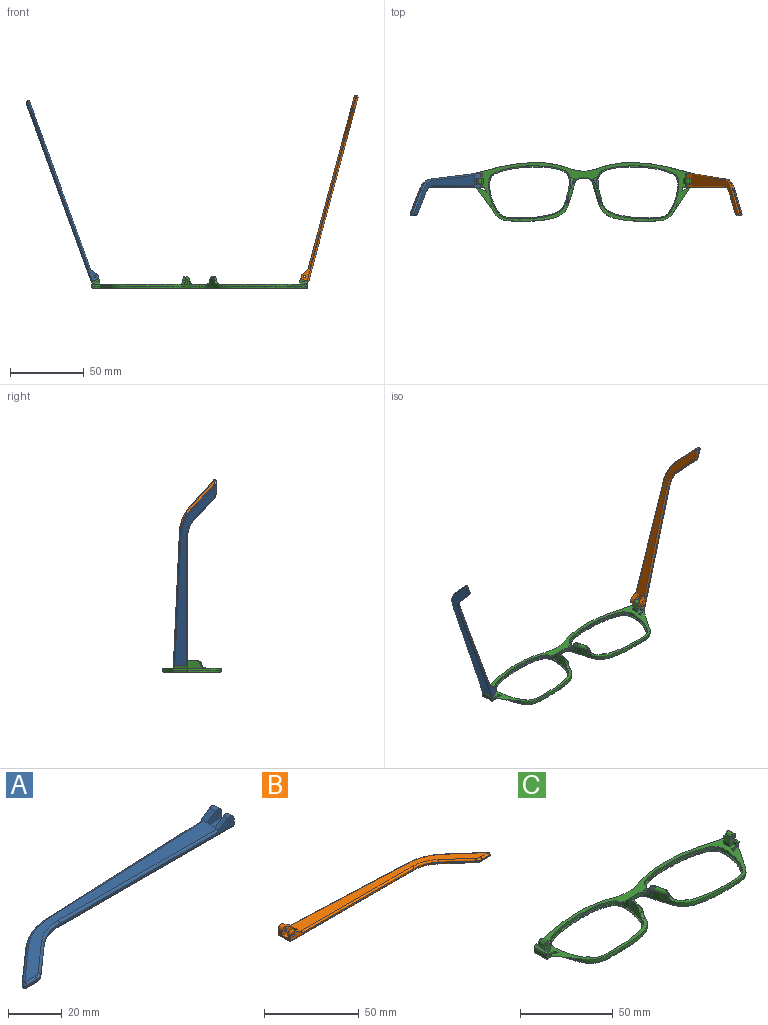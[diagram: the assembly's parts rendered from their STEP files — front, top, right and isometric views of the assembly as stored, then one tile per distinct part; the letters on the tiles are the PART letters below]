
ASSEMBLY  parts=3 mates=2
PART A: 43 faces, bbox 130.2x29.5x5.9 mm
  f0: plane 9.62x3.72mm, normal (1,0,0), area 24.7mm2, adj f1,f3,f4,f5,f10,f16,f18,f28
  f1: cylinder r=2.2mm len=3.45mm, axis (0,-1,0), area 11mm2, adj f0,f2,f4,f37
  f2: plane 6.01x3.91mm, normal (-0.55,0,0.84), area 12.7mm2, adj f1,f4,f9,f19,f37
  f3: plane 2.26x0.1mm, normal (0,0,1), area 0.1mm2, adj f0,f5,f18
  f4: plane 92.1x4.9mm, normal (0,-1,0), area 79.9mm2, adj f0,f1,f2,f14,f19,f36,f42
  f5: plane 93.42x4.13mm, normal (-0.04,1,0), area 64.8mm2, adj f0,f3,f11,f15,f17,f27,f28
  f6: plane 17.82x15.72mm, normal (-0.66,0.75,0), area 14.3mm2, adj f11,f12,f25,f30
  f7: plane 5.46x0.6mm, normal (0,-1,0), area 3.3mm2, adj f12,f13,f23,f32
  f8: plane 14.99x13.23mm, normal (0.66,-0.75,0), area 12mm2, adj f13,f14,f21,f34
  f9: plane 121.18x26.73mm, normal (0,0,1), area 627.7mm2, adj f2,f17,f19,f20,f21,f22,f23,f25
  f10: plane 129.1x27.08mm, normal (0,0,-1), area 686.5mm2, adj f0,f28,f29,f30,f32,f33,f34,f35
  f11: cylinder r=30mm len=18.52mm, axis (0,0,-1), area 12.2mm2, adj f5,f6,f26,f29
  f12: cylinder r=1mm len=1.75mm, axis (0,0,-1), area 1.5mm2, adj f6,f7,f24,f31
  f13: cylinder r=5mm len=3.31mm, axis (0,0,-1), area 2.2mm2, adj f7,f8,f22,f33
  f14: cylinder r=20mm len=13.23mm, axis (0,0,1), area 8.7mm2, adj f4,f8,f20,f35
  f15: plane 5.66x0.25mm, normal (0,0,-1), area 0.7mm2, adj f5,f17,f18
  f16: cylinder r=2.2mm len=3.45mm, axis (0,-1,0), area 14.8mm2, adj f0,f17,f18,f38
  f17: plane 6.01x3.91mm, normal (-0.55,0,0.84), area 16.9mm2, adj f5,f9,f15,f16,f18,f27,f38
  f18: plane 7.92x3.3mm, normal (0,1,0), area 15.9mm2, adj f0,f3,f15,f16,f17,f41
  f19: cylinder r=1mm len=84.18mm, axis (-1,0,0), area 131.4mm2, adj f2,f4,f9,f20
  f20: torus R=21mm, axis (0,0,1), area 23.1mm2, adj f9,f14,f19,f21
  f21: cylinder r=1mm len=15.65mm, axis (-0.75,-0.66,0), area 31.4mm2, adj f8,f9,f20,f22
  f22: torus R=4mm, axis (0,0,1), area 5.3mm2, adj f9,f13,f21,f23
  f23: cylinder r=1mm len=5.46mm, axis (-1,0,0), area 8.6mm2, adj f7,f9,f22,f24
  f24: sphere r=1mm, area 2.4mm2, adj f12,f23,f25
  f25: cylinder r=1mm len=18.48mm, axis (0.75,0.66,0), area 37.3mm2, adj f6,f9,f24,f26
  f26: torus R=29mm, axis (0,0,1), area 31.6mm2, adj f9,f11,f25,f27
  f27: cylinder r=1mm len=85.5mm, axis (1,0.04,0), area 133.5mm2, adj f5,f9,f17,f26
  f28: cylinder r=1mm len=93.46mm, axis (-1,-0.04,0), area 146.9mm2, adj f0,f5,f10,f29
  f29: torus R=29mm, axis (0,0,1), area 31.6mm2, adj f10,f11,f28,f30
  f30: cylinder r=1mm len=18.48mm, axis (-0.75,-0.66,0), area 37.3mm2, adj f6,f10,f29,f31
  f31: sphere r=1mm, area 2.4mm2, adj f12,f30,f32
  f32: cylinder r=1mm len=5.46mm, axis (1,0,0), area 8.6mm2, adj f7,f10,f31,f33
  f33: torus R=4mm, axis (0,0,1), area 5.3mm2, adj f10,f13,f32,f34
  f34: cylinder r=1mm len=15.65mm, axis (0.75,0.66,0), area 31.4mm2, adj f8,f10,f33,f35
  f35: torus R=21mm, axis (0,0,1), area 23.1mm2, adj f10,f14,f34,f36
  f36: cylinder r=1mm len=92.1mm, axis (1,0,0), area 144.7mm2, adj f0,f4,f10,f35
  f37: plane 7.92x4.7mm, normal (0,1,0), area 27mm2, adj f0,f1,f2,f39,f40,f42
  f38: plane 7.92x4.7mm, normal (0,-1,0), area 27mm2, adj f0,f16,f17,f39,f40,f41
  f39: plane 7.92x4.1mm, normal (0,0,1), area 32.5mm2, adj f0,f37,f38,f40
  f40: plane 4.1x1.4mm, normal (1,0,0), area 5.7mm2, adj f9,f37,f38,f39
  f41: cylinder r=0.5mm len=3.1mm, axis (0,-1,0), area 9.7mm2, adj f18,f38
  f42: cylinder r=0.5mm len=2.3mm, axis (0,-1,0), area 7.2mm2, adj f4,f37
PART B: 43 faces, bbox 130.2x29.5x5.9 mm
  f0: plane 9.62x3.72mm, normal (-1,0,0), area 24.7mm2, adj f1,f3,f4,f5,f10,f16,f18,f28
  f1: cylinder r=2.2mm len=3.45mm, axis (0,-1,0), area 11mm2, adj f0,f2,f4,f37
  f2: plane 6.01x3.91mm, normal (0.55,0,0.84), area 12.7mm2, adj f1,f4,f9,f19,f37
  f3: plane 2.26x0.1mm, normal (0,0,1), area 0.1mm2, adj f0,f5,f18
  f4: plane 92.1x4.9mm, normal (0,-1,0), area 78.2mm2, adj f0,f1,f2,f14,f19,f36,f42
  f5: plane 93.42x4.13mm, normal (0.04,1,0), area 64.8mm2, adj f0,f3,f11,f15,f17,f27,f28
  f6: plane 17.82x15.72mm, normal (0.66,0.75,0), area 14.3mm2, adj f11,f12,f25,f30
  f7: plane 5.46x0.6mm, normal (0,-1,0), area 3.3mm2, adj f12,f13,f23,f32
  f8: plane 14.99x13.23mm, normal (-0.66,-0.75,0), area 12mm2, adj f13,f14,f21,f34
  f9: plane 121.18x26.73mm, normal (0,0,1), area 627.7mm2, adj f2,f17,f19,f20,f21,f22,f23,f25
  f10: plane 129.1x27.08mm, normal (0,0,-1), area 686.5mm2, adj f0,f28,f29,f30,f32,f33,f34,f35
  f11: cylinder r=30mm len=18.52mm, axis (0,0,-1), area 12.2mm2, adj f5,f6,f26,f29
  f12: cylinder r=1mm len=1.75mm, axis (0,0,-1), area 1.5mm2, adj f6,f7,f24,f31
  f13: cylinder r=5mm len=3.31mm, axis (0,0,-1), area 2.2mm2, adj f7,f8,f22,f33
  f14: cylinder r=20mm len=13.23mm, axis (0,0,1), area 8.7mm2, adj f4,f8,f20,f35
  f15: plane 5.66x0.25mm, normal (0,0,-1), area 0.7mm2, adj f5,f17,f18
  f16: cylinder r=2.2mm len=3.45mm, axis (0,-1,0), area 14.8mm2, adj f0,f17,f18,f38
  f17: plane 6.01x3.91mm, normal (0.55,0,0.84), area 16.9mm2, adj f5,f9,f15,f16,f18,f27,f38
  f18: plane 7.92x3.3mm, normal (0,1,0), area 14.3mm2, adj f0,f3,f15,f16,f17,f41
  f19: cylinder r=1mm len=84.18mm, axis (1,0,0), area 131.4mm2, adj f2,f4,f9,f20
  f20: torus R=21mm, axis (0,0,1), area 23.1mm2, adj f9,f14,f19,f21
  f21: cylinder r=1mm len=15.65mm, axis (0.75,-0.66,0), area 31.4mm2, adj f8,f9,f20,f22
  f22: torus R=4mm, axis (0,0,1), area 5.3mm2, adj f9,f13,f21,f23
  f23: cylinder r=1mm len=5.46mm, axis (1,0,0), area 8.6mm2, adj f7,f9,f22,f24
  f24: sphere r=1mm, area 2.4mm2, adj f12,f23,f25
  f25: cylinder r=1mm len=18.48mm, axis (-0.75,0.66,0), area 37.3mm2, adj f6,f9,f24,f26
  f26: torus R=29mm, axis (0,0,1), area 31.6mm2, adj f9,f11,f25,f27
  f27: cylinder r=1mm len=85.5mm, axis (-1,0.04,0), area 133.5mm2, adj f5,f9,f17,f26
  f28: cylinder r=1mm len=93.46mm, axis (1,-0.04,0), area 146.9mm2, adj f0,f5,f10,f29
  f29: torus R=29mm, axis (0,0,1), area 31.6mm2, adj f10,f11,f28,f30
  f30: cylinder r=1mm len=18.48mm, axis (0.75,-0.66,0), area 37.3mm2, adj f6,f10,f29,f31
  f31: sphere r=1mm, area 2.4mm2, adj f12,f30,f32
  f32: cylinder r=1mm len=5.46mm, axis (-1,0,0), area 8.6mm2, adj f7,f10,f31,f33
  f33: torus R=4mm, axis (0,0,1), area 5.3mm2, adj f10,f13,f32,f34
  f34: cylinder r=1mm len=15.65mm, axis (-0.75,0.66,0), area 31.4mm2, adj f8,f10,f33,f35
  f35: torus R=21mm, axis (0,0,1), area 23.1mm2, adj f10,f14,f34,f36
  f36: cylinder r=1mm len=92.1mm, axis (-1,0,0), area 144.7mm2, adj f0,f4,f10,f35
  f37: plane 7.92x4.7mm, normal (0,1,0), area 25.4mm2, adj f0,f1,f2,f39,f40,f42
  f38: plane 7.92x4.7mm, normal (0,-1,0), area 25.4mm2, adj f0,f16,f17,f39,f40,f41
  f39: plane 7.92x4.1mm, normal (0,0,1), area 32.5mm2, adj f0,f37,f38,f40
  f40: plane 4.1x1.4mm, normal (-1,0,0), area 5.7mm2, adj f9,f37,f38,f39
  f41: cylinder r=0.88mm len=3.1mm, axis (0,-1,0), area 17mm2, adj f18,f38
  f42: cylinder r=0.88mm len=2.3mm, axis (0,-1,0), area 12.6mm2, adj f4,f37
PART C: 118 faces, bbox 148.1x40.9x18 mm
  f0: bspline ~1.82x1.22mm, area 0.7mm2, adj f2,f7,f37,f52
  f1: plane 147.73x40.5mm, normal (0,0,1), area 772.9mm2, adj f4,f5,f6,f7,f8,f12,f20,f23
  f2: bspline ~5.39x4.93mm, area 12.7mm2, adj f0,f7,f37,f41,f43,f52,f53
  f3: plane 4.46x1.45mm, normal (0,0,1), area 0.1mm2, adj f7,f38
  f4: plane 1.23x0.04mm, normal (0,0,1), area 0mm2, adj f1,f7,f22
  f5: plane 6.97x5.07mm, normal (0,1,0), area 22.7mm2, adj f1,f20,f21,f25,f27,f28,f30,f31
  f6: plane 3.2x2.36mm, normal (0,-1,0), area 5.7mm2, adj f1,f20,f26,f29
  f7: extruded ~73.26x39.84mm, area 292.7mm2, adj f0,f1,f2,f3,f4,f8,f13,f14
  f8: extruded ~35.39x5.69mm, area 72.2mm2, adj f1,f7,f18,f67
  f9: plane 144.78x37.85mm, normal (0,0,-1), area 478.1mm2, adj f13,f15,f17,f18,f19,f71,f73,f75
  f10: plane 56.31x36.53mm, normal (0,0,1), area 124.8mm2, adj f11,f19
  f11: extruded ~55.63x36.1mm, area 160.7mm2, adj f10,f12
  f12: extruded ~55.63x36.1mm, area 220.4mm2, adj f1,f11,f39,f40,f41,f42,f43,f44
  f13: bspline ~73.27x30.39mm, area 161.7mm2, adj f7,f9,f14,f71
  f14: bspline ~1x1mm, area 0.8mm2, adj f7,f13,f15
  f15: bspline ~8.99x1.23mm, area 12.6mm2, adj f7,f9,f14,f16
  f16: bspline ~1.04x1mm, area 0.7mm2, adj f7,f15,f17
  f17: bspline ~45.86x8.59mm, area 59.8mm2, adj f7,f9,f16,f18
  f18: bspline ~37.01x6.7mm, area 56.6mm2, adj f8,f9,f17,f76
  f19: bspline ~56.15x36.68mm, area 237.6mm2, adj f9,f10
  f20: plane 4x2.36mm, normal (-1,0,0), area 9.5mm2, adj f1,f5,f6,f21
  f21: plane 4x0.02mm, normal (0.34,0,0.94), area 0.1mm2, adj f5,f20,f28
  f22: plane 2.76x2.53mm, normal (0,-1,0), area 3.9mm2, adj f4,f26,f27,f35,f56
  f23: plane 7.67x1.6mm, normal (0.94,0,-0.34), area 13mm2, adj f1,f35,f36,f56
  f24: plane 2.1x1.69mm, normal (0,1,0), area 2.8mm2, adj f1,f25,f27,f36,f56
  f25: plane 3.3x2.1mm, normal (-1,0,0), area 6.9mm2, adj f1,f5,f24,f27
  f26: plane 2.35x2.1mm, normal (-1,0,0), area 4.9mm2, adj f1,f6,f22,f27,f29
  f27: plane 9.65x1.24mm, normal (0,0,1), area 8.2mm2, adj f5,f22,f24,f25,f26,f29,f30,f56
  f28: plane 4x3.31mm, normal (-0.94,0,0.34), area 14.1mm2, adj f5,f21,f29,f32
  f29: plane 5.77x5.06mm, normal (0,-1,0), area 17mm2, adj f6,f26,f27,f28,f30,f31,f32,f33
  f30: plane 4x2.21mm, normal (0.94,0,-0.34), area 9.4mm2, adj f5,f27,f29,f33
  f31: plane 4x0.01mm, normal (0.34,0,0.94), area 0mm2, adj f5,f29,f32,f33
  f32: cylinder r=1.98mm len=4mm, axis (0,1,0), area 12.4mm2, adj f5,f28,f29,f31
  f33: cylinder r=1.98mm len=4mm, axis (0,-1,0), area 12.4mm2, adj f5,f29,f30,f31
  f34: cylinder r=0.88mm len=4mm, axis (0,-1,0), area 22mm2, adj f5,f29
  f35: cone r=1mm half-angle=20deg, axis (0,0,1), area 2.3mm2, adj f1,f22,f23,f56
  f36: cylinder r=1mm len=2.28mm, axis (-0.34,0,-0.94), area 3mm2, adj f1,f23,f24,f56
  f37: extruded ~3.67x3.11mm, area 5.9mm2, adj f0,f2,f7,f59
  f38: extruded ~4.44x3.32mm, area 15.1mm2, adj f3,f7,f42,f43,f55
  f39: extruded ~4.98x1.36mm, area 6.6mm2, adj f12,f41
  f40: plane 3.63x0.97mm, normal (0,0,1), area 0.3mm2, adj f12,f41,f43
  f41: bspline ~15.5x15.35mm, area 6.4mm2, adj f2,f12,f39,f40,f54
  f42: bspline ~7.26x7.26mm, area 6.3mm2, adj f12,f38,f43,f55
  f43: bspline ~10.29x4.84mm, area 21.4mm2, adj f2,f7,f12,f38,f40,f42
  f44: plane 2.88x1.51mm, normal (0,0,-1), area 1.8mm2, adj f12,f45
  f45: cylinder r=2.28mm len=2.86mm, axis (0,0,1), area 1.8mm2, adj f1,f12,f44,f54
  f46: plane 2.5x1.83mm, normal (0,0,-1), area 1.7mm2, adj f12,f47
  f47: cylinder r=2.28mm len=2.47mm, axis (0,0,1), area 1.7mm2, adj f1,f12,f46
  f48: plane 1.79x1.31mm, normal (0,0,-1), area 0.9mm2, adj f12,f49
  f49: cylinder r=1.3mm len=1.78mm, axis (0,0,1), area 1.3mm2, adj f1,f12,f48
  f50: plane 1.95x1.68mm, normal (0,0,-1), area 1.5mm2, adj f12,f51
  f51: cylinder r=1.3mm len=1.93mm, axis (0,0,1), area 1.5mm2, adj f1,f12,f50
  f52: bspline ~2.66x2.04mm, area 1.9mm2, adj f0,f2,f7,f53,f58
  f53: bspline ~3.55x3.47mm, area 3.7mm2, adj f1,f2,f52,f54,f58
  f54: bspline ~5.1x3.97mm, area 7.6mm2, adj f1,f12,f41,f45,f53
  f55: bspline ~3.7x3.66mm, area 7.8mm2, adj f1,f7,f12,f38,f42
  f56: plane 9.71x1.44mm, normal (0.34,0,0.94), area 13.9mm2, adj f22,f23,f24,f27,f35,f36
  f57: bspline ~6.38x2.14mm, area 2.6mm2, adj f1,f7,f58,f115
  f58: bspline ~2.1x1.46mm, area 0.6mm2, adj f7,f52,f53,f57
  f59: bspline ~5.24x1.75mm, area 0mm2, adj f7,f37
  f60: bspline ~2.19x1.4mm, area 0.7mm2, adj f61,f66,f95,f110
  f61: bspline ~6.1x4.93mm, area 12.6mm2, adj f60,f66,f95,f99,f101,f110,f111
  f62: plane 4.46x1.45mm, normal (0,0,1), area 0.1mm2, adj f66,f96
  f63: plane 1.23x0.04mm, normal (0,0,1), area 0mm2, adj f1,f66,f80
  f64: plane 6.97x5.07mm, normal (0,1,0), area 22.7mm2, adj f1,f78,f79,f83,f85,f86,f88,f89
  f65: plane 3.2x2.36mm, normal (0,-1,0), area 5.7mm2, adj f1,f78,f84,f87
  f66: extruded ~73.26x39.84mm, area 292.7mm2, adj f1,f7,f60,f61,f62,f63,f67,f71
  f67: extruded ~35.39x5.69mm, area 72.2mm2, adj f1,f8,f66,f76
  f68: plane 56.31x36.53mm, normal (0,0,1), area 124.8mm2, adj f69,f77
  f69: extruded ~55.63x36.1mm, area 160.7mm2, adj f68,f70
  f70: extruded ~55.63x36.1mm, area 220.4mm2, adj f1,f69,f97,f98,f99,f100,f101,f102
  f71: bspline ~73.83x30.39mm, area 161.7mm2, adj f9,f13,f66,f72
  f72: bspline ~1x1mm, area 0.8mm2, adj f66,f71,f73
  f73: bspline ~8.99x1.23mm, area 12.6mm2, adj f9,f66,f72,f74
  f74: bspline ~1.04x1mm, area 0.8mm2, adj f66,f73,f75
  f75: bspline ~45.86x8.59mm, area 59.8mm2, adj f9,f66,f74,f76
  f76: bspline ~37.01x6.7mm, area 56.6mm2, adj f9,f18,f67,f75
  f77: bspline ~56.15x36.68mm, area 237.6mm2, adj f9,f68
  f78: plane 4x2.36mm, normal (1,0,0), area 9.5mm2, adj f1,f64,f65,f79
  f79: plane 4x0.02mm, normal (-0.34,0,0.94), area 0.1mm2, adj f64,f78,f86
  f80: plane 2.76x2.53mm, normal (0,-1,0), area 3.9mm2, adj f63,f84,f85,f93,f114
  f81: plane 7.67x1.6mm, normal (-0.94,0,-0.34), area 13mm2, adj f1,f93,f94,f114
  f82: plane 2.1x1.69mm, normal (0,1,0), area 2.8mm2, adj f1,f83,f85,f94,f114
  f83: plane 3.3x2.1mm, normal (1,0,0), area 6.9mm2, adj f1,f64,f82,f85
  f84: plane 2.35x2.1mm, normal (1,0,0), area 4.9mm2, adj f1,f65,f80,f85,f87
  f85: plane 9.65x1.24mm, normal (0,0,1), area 8.2mm2, adj f64,f80,f82,f83,f84,f87,f88,f114
  f86: plane 4x3.31mm, normal (0.94,0,0.34), area 14.1mm2, adj f64,f79,f87,f90
  f87: plane 5.77x5.06mm, normal (0,-1,0), area 17mm2, adj f65,f84,f85,f86,f88,f89,f90,f91
  f88: plane 4x2.21mm, normal (-0.94,0,-0.34), area 9.4mm2, adj f64,f85,f87,f91
  f89: plane 4x0.01mm, normal (-0.34,0,0.94), area 0mm2, adj f64,f87,f90,f91
  f90: cylinder r=1.98mm len=4mm, axis (0,1,0), area 12.4mm2, adj f64,f86,f87,f89
  f91: cylinder r=1.98mm len=4mm, axis (0,-1,0), area 12.4mm2, adj f64,f87,f88,f89
  f92: cylinder r=0.88mm len=4mm, axis (0,-1,0), area 22mm2, adj f64,f87
  f93: cone r=1mm half-angle=20deg, axis (0,0,1), area 2.3mm2, adj f1,f80,f81,f114
  f94: cylinder r=1mm len=2.28mm, axis (0.34,0,-0.94), area 3mm2, adj f1,f81,f82,f114
  f95: extruded ~3.67x3.11mm, area 5.9mm2, adj f60,f61,f66,f117
  f96: extruded ~4.44x3.32mm, area 15.1mm2, adj f62,f66,f100,f101,f113
  f97: extruded ~4.98x1.36mm, area 6.6mm2, adj f70,f99
  f98: plane 3.63x0.97mm, normal (0,0,1), area 0.3mm2, adj f70,f99,f101
  f99: bspline ~15.5x15.35mm, area 6.4mm2, adj f61,f70,f97,f98,f112
  f100: bspline ~7.26x7.26mm, area 6.2mm2, adj f70,f96,f101,f113
  f101: bspline ~10.29x4.84mm, area 21.5mm2, adj f61,f66,f70,f96,f98,f100
  f102: plane 2.88x1.51mm, normal (0,0,-1), area 1.8mm2, adj f70,f103
  f103: cylinder r=2.28mm len=2.86mm, axis (0,0,1), area 1.8mm2, adj f1,f70,f102,f112
  f104: plane 2.5x1.83mm, normal (0,0,-1), area 1.7mm2, adj f70,f105
  f105: cylinder r=2.28mm len=2.47mm, axis (0,0,1), area 1.7mm2, adj f1,f70,f104
  f106: plane 1.79x1.31mm, normal (0,0,-1), area 0.9mm2, adj f70,f107
  f107: cylinder r=1.3mm len=1.78mm, axis (0,0,1), area 1.3mm2, adj f1,f70,f106
  f108: plane 1.95x1.68mm, normal (0,0,-1), area 1.5mm2, adj f70,f109
  f109: cylinder r=1.3mm len=1.93mm, axis (0,0,1), area 1.5mm2, adj f1,f70,f108
  f110: bspline ~2.65x2.03mm, area 1.9mm2, adj f60,f61,f66,f111,f116
  f111: bspline ~3.55x3.47mm, area 3.7mm2, adj f1,f61,f110,f112,f116
  f112: bspline ~4.88x3.94mm, area 7.6mm2, adj f1,f70,f99,f103,f111
  f113: bspline ~3.7x3.66mm, area 7.8mm2, adj f1,f66,f70,f96,f100
  f114: plane 9.71x1.44mm, normal (-0.34,0,0.94), area 13.9mm2, adj f80,f81,f82,f85,f93,f94
  f115: bspline ~6.38x2.14mm, area 2.6mm2, adj f1,f57,f66,f116
  f116: bspline ~2.1x1.46mm, area 0.6mm2, adj f66,f110,f111,f115
  f117: bspline ~5.24x1.75mm, area 0mm2, adj f66,f95
PLACE A rot(axis=(0,1,0),70deg) t=(-84.77,-5.75,56)mm
PLACE B rot(axis=(0,-1,0),75deg) t=(68.2,-5.75,-61.61)mm
PLACE C t=(10.15,-1.13,-5.77)mm
MATE revolute A.f1 <-> C.f90  axis (0,-1,0) through (-60.89,2.72,1.22)mm
MATE revolute B.f41 <-> C.f33  axis (0,-1,0) through (81.2,2.72,1.21)mm
